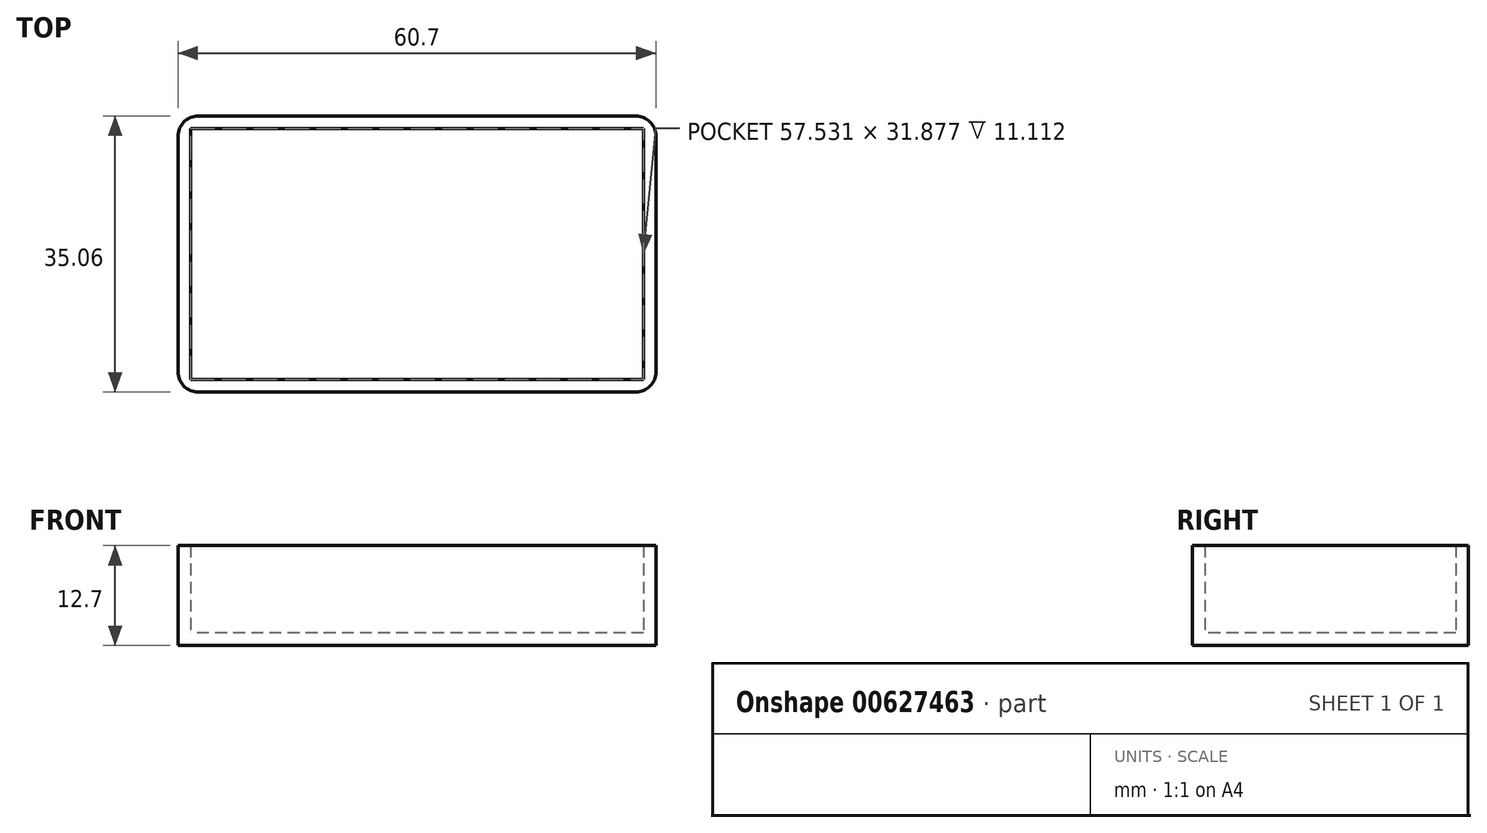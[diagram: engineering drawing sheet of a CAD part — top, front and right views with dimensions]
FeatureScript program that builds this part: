
annotation { "Feature Type Name" : "Feature", "Feature Type Description" : "" }
export const myFeature = defineFeature(function(context is Context, id is Id, definition is map)
    precondition{}
    {
        {
            var Q0;
            Q0=qCreatedBy(makeId("Top.planeOp"),FACE);
            var sketch = newSketch(context, id + "F0", { "sketchPlane" : qUnion([Q0])});
            skLineSegment(sketch, "E0.bottom", {"start": v(30.35, 17.53) * mm, "end": v(-30.35, 17.53) * mm});
            skLineSegment(sketch, "E0.top", {"start": v(30.35, -17.53) * mm, "end": v(-30.35, -17.53) * mm});
            skLineSegment(sketch, "E0.left", {"start": v(30.35, 17.53) * mm, "end": v(30.35, -17.53) * mm});
            skLineSegment(sketch, "E0.right", {"start": v(-30.35, 17.53) * mm, "end": v(-30.35, -17.53) * mm});
            skPoint(sketch, "E0.middle", {"position": v(0, 0) * mm});
            skSolve(sketch);
        }
        {
            var Q0;
            Q0 = qSketchRegion(id + "F0", true);
            extrude(context, id + "F1", {"entities" : qUnion([Q0]), "depth" : 12.7 * mm, "offsetDistance" : 25.4 * mm});
        }
        {
            var Q0;
            Q0=makeQuery(id+"F1.opExtrude","CAP_FACE",FACE,{"disambiguationData":[OSD([sQuery(id+"F0.wireOp",EDGE,"E0.bottom"),sQuery(id+"F0.wireOp",EDGE,"E0.top"),sQuery(id+"F0.wireOp",EDGE,"E0.left"),sQuery(id+"F0.wireOp",EDGE,"E0.right")])],"isStart":false});
            shell(context, id + "F2", {"entities" : qUnion([Q0]), "thickness" : 1.59 * mm});
        }
        {
            var Q0;
            Q0=makeQuery(id+"F1.opExtrude","SWEPT_EDGE",EDGE,{"disambiguationData":[OSD([sQuery(id+"F0.wireOp",EDGE,"E0.top"),sQuery(id+"F0.wireOp",EDGE,"E0.right")])]});
            var Q1;
            Q1=makeQuery(id+"F1.opExtrude","SWEPT_EDGE",EDGE,{"disambiguationData":[OSD([sQuery(id+"F0.wireOp",EDGE,"E0.bottom"),sQuery(id+"F0.wireOp",EDGE,"E0.right")])]});
            var Q2;
            Q2=makeQuery(id+"F1.opExtrude","SWEPT_EDGE",EDGE,{"disambiguationData":[OSD([sQuery(id+"F0.wireOp",EDGE,"E0.top"),sQuery(id+"F0.wireOp",EDGE,"E0.left")])]});
            var Q3;
            Q3=makeQuery(id+"F1.opExtrude","SWEPT_EDGE",EDGE,{"disambiguationData":[OSD([sQuery(id+"F0.wireOp",EDGE,"E0.bottom"),sQuery(id+"F0.wireOp",EDGE,"E0.left")])]});
            fillet(context, id + "F3", {"entities" : qUnion([Q0, Q1, Q2, Q3]), "radius" : 2.54 * mm, "tangentPropagation" : true, "allowEdgeOverflow" : false});
        }
    });
